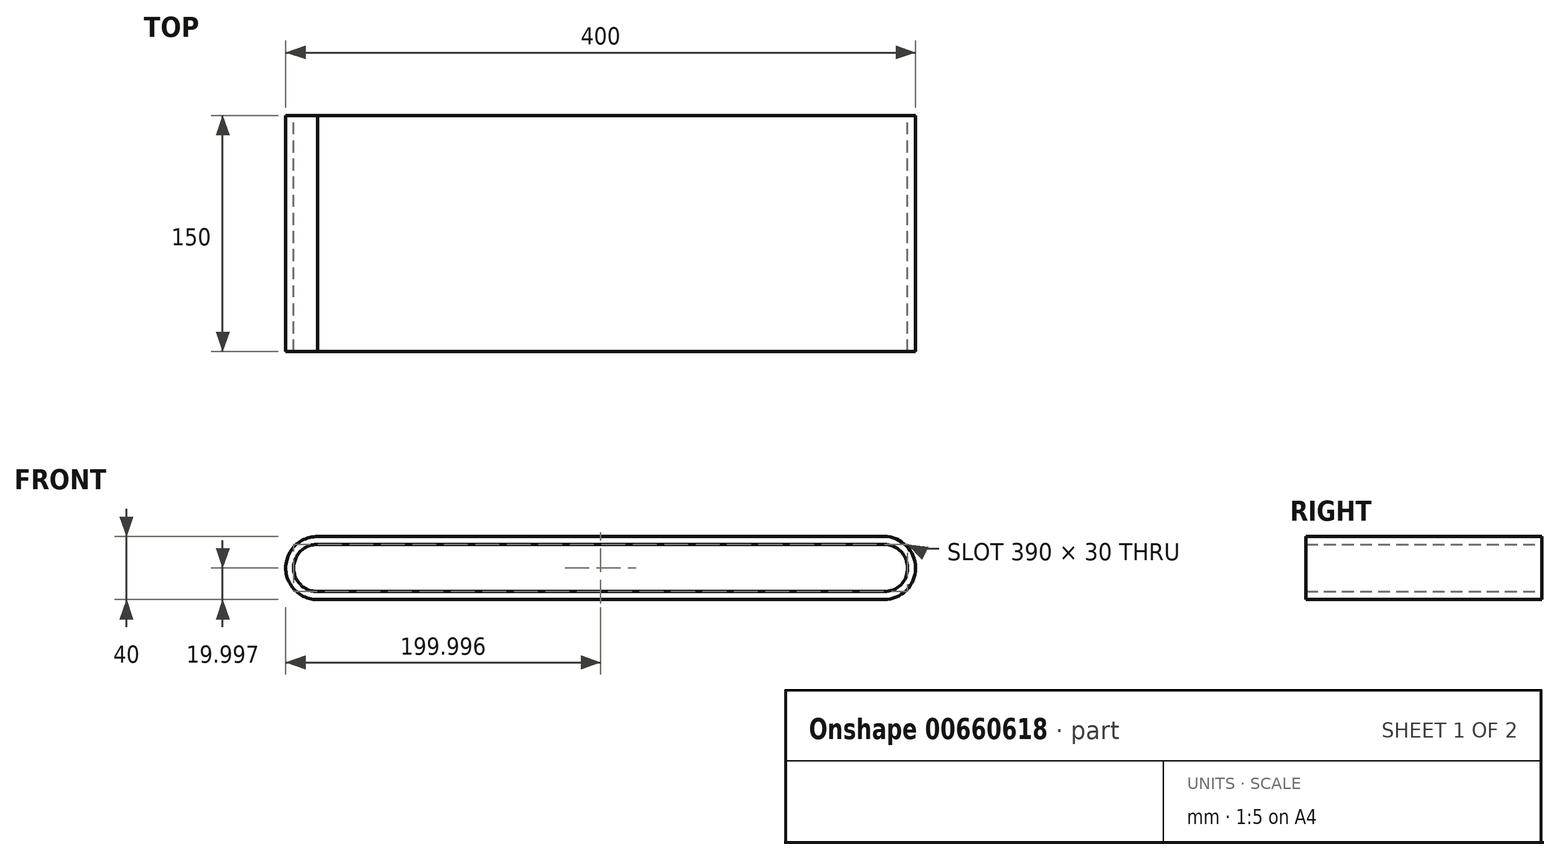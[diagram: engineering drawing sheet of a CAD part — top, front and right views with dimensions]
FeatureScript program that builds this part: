
annotation { "Feature Type Name" : "Feature", "Feature Type Description" : "" }
export const myFeature = defineFeature(function(context is Context, id is Id, definition is map)
    precondition{}
    {
        {
            var Q0;
            Q0=qCreatedBy(makeId("Front.planeOp"),FACE);
            var sketch = newSketch(context, id + "F0", { "sketchPlane" : qUnion([Q0])});
            skArc(sketch, "E0", {"start": v(-274.99, 20.85) * mm, "mid": v(-290.3, 6) * mm, "end": v(-275.3, -9.14) * mm});
            skArc(sketch, "E1", {"start": v(84.7, -9.14) * mm, "mid": v(99.7, 5.86) * mm, "end": v(84.7, 20.86) * mm});
            skArc(sketch, "E2.0", {"start": v(-274.99, 25.85) * mm, "mid": v(-295.3, 6) * mm, "end": v(-275.3, -14.14) * mm});
            skArc(sketch, "E3.0", {"start": v(84.7, -14.14) * mm, "mid": v(104.7, 5.86) * mm, "end": v(84.7, 25.86) * mm});
            skLineSegment(sketch, "E4", {"start": v(-274.99, 25.85) * mm, "end": v(84.7, 25.86) * mm});
            skLineSegment(sketch, "E5", {"start": v(84.7, -14.14) * mm, "end": v(-275.3, -14.14) * mm});
            skLineSegment(sketch, "E6", {"start": v(-274.99, 20.85) * mm, "end": v(84.7, 20.86) * mm});
            skLineSegment(sketch, "E7", {"start": v(84.7, -9.14) * mm, "end": v(-275.3, -9.14) * mm});
            skSolve(sketch);
        }
        {
            var Q0;
            Q0=qSketchRegion(id+"F0",true);
            extrude(context, id + "F1", {"entities" : qUnion([Q0]), "depth" : 150 * mm, "offsetDistance" : 25 * mm});
        }
    });
